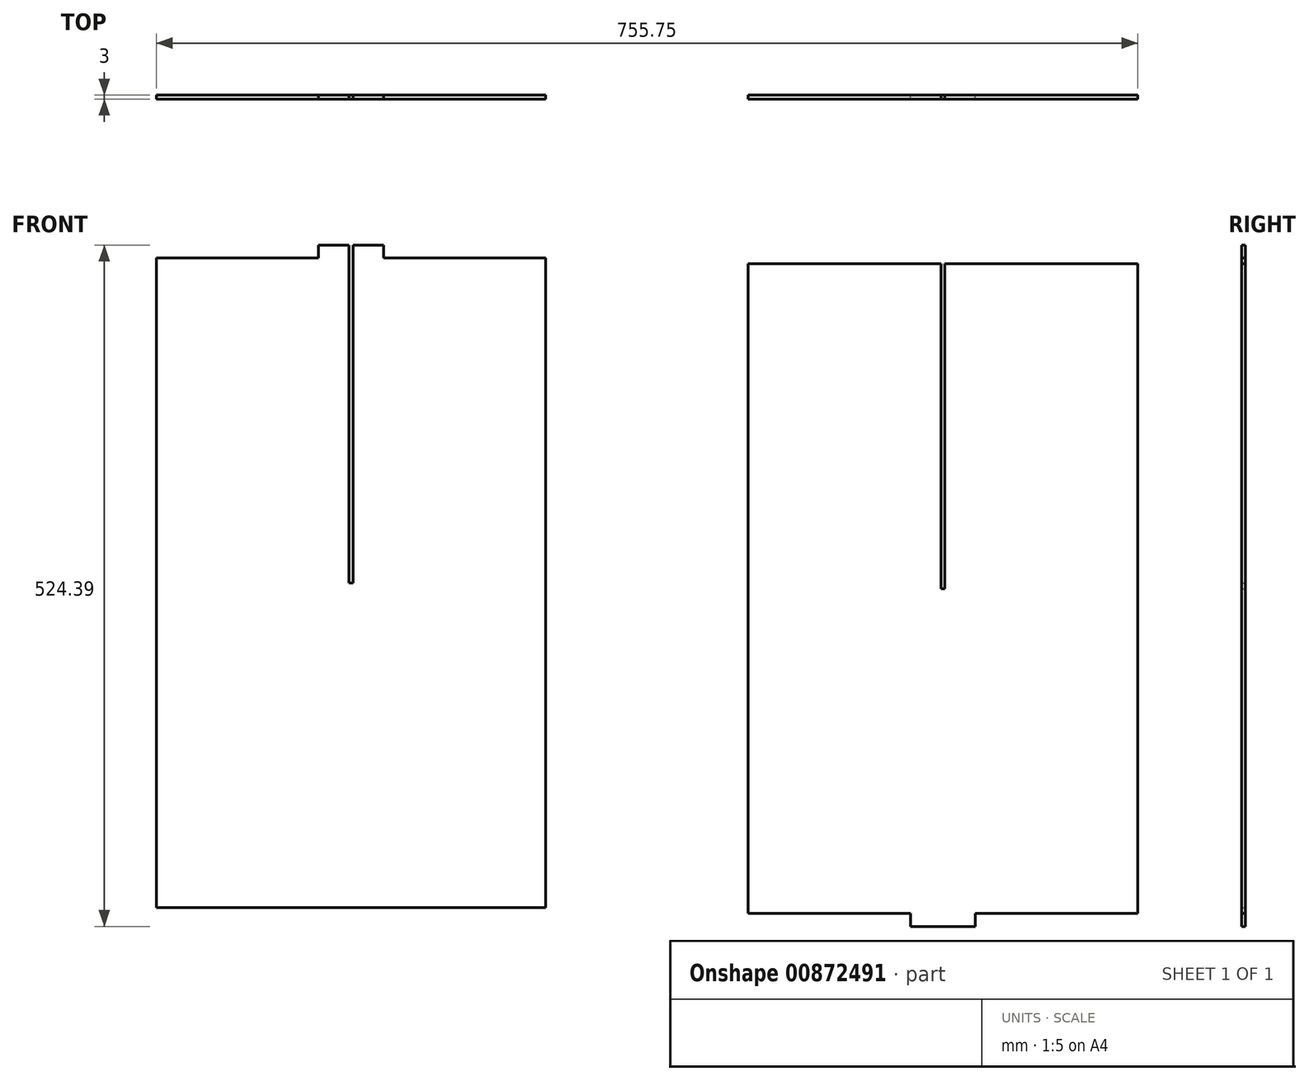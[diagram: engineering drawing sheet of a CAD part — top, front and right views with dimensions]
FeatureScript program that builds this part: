
annotation { "Feature Type Name" : "Feature", "Feature Type Description" : "" }
export const myFeature = defineFeature(function(context is Context, id is Id, definition is map)
    precondition{}
    {
        {
            var Q0;
            Q0=qCreatedBy(makeId("Front.planeOp"),FACE);
            var sketch = newSketch(context, id + "F0", { "sketchPlane" : qUnion([Q0])});
            skLineSegment(sketch, "E0.bottom", {"start": v(-150, -250) * mm, "end": v(150, -250) * mm});
            skLineSegment(sketch, "E0.top", {"start": v(-150, 250) * mm, "end": v(-25, 250) * mm});
            skLineSegment(sketch, "E0.left", {"start": v(-150, -250) * mm, "end": v(-150, 250) * mm});
            skLineSegment(sketch, "E0.right", {"start": v(150, -250) * mm, "end": v(150, 250) * mm});
            skPoint(sketch, "E0.middle", {"position": v(0, 0) * mm});
            skLineSegment(sketch, "E1.left", {"start": v(-1.5, 250) * mm, "end": v(-1.5, 250) * mm});
            skLineSegment(sketch, "E2.bottom", {"start": v(-1.5, 0) * mm, "end": v(1.5, 0) * mm});
            skLineSegment(sketch, "E2.left", {"start": v(-1.5, 0) * mm, "end": v(-1.5, 0) * mm});
            skLineSegment(sketch, "E2.right", {"start": v(1.5, 0) * mm, "end": v(1.5, 0) * mm});
            skLineSegment(sketch, "E3", {"start": v(-1.5, 250) * mm, "end": v(-1.5, 0) * mm});
            skLineSegment(sketch, "E4", {"start": v(1.5, 250) * mm, "end": v(1.5, 0) * mm});
            skLineSegment(sketch, "E5.trimOffspring", {"start": v(25, 250) * mm, "end": v(150, 250) * mm});
            skLineSegment(sketch, "E6.top", {"start": v(25, 260) * mm, "end": v(1.5, 260) * mm});
            skLineSegment(sketch, "E6.left", {"start": v(25, 260) * mm, "end": v(25, 250) * mm});
            skLineSegment(sketch, "E6.right", {"start": v(-25, 260) * mm, "end": v(-25, 250) * mm});
            skPoint(sketch, "E6.middle", {"position": v(0, 255) * mm});
            skPoint(sketch, "E1.right.start.orphan", {"position": v(1.5, 255) * mm});
            skLineSegment(sketch, "E7", {"start": v(-1.5, 250) * mm, "end": v(-1.5, 260) * mm});
            skLineSegment(sketch, "E8", {"start": v(1.5, 250) * mm, "end": v(1.5, 260) * mm});
            skLineSegment(sketch, "E9.trimOffspring", {"start": v(-1.5, 260) * mm, "end": v(-25, 260) * mm});
            skLineSegment(sketch, "E10.bottom", {"start": v(305.75, -254.39) * mm, "end": v(430.75, -254.39) * mm});
            skLineSegment(sketch, "E10.top", {"start": v(305.75, 245.61) * mm, "end": v(430.75, 245.61) * mm});
            skLineSegment(sketch, "E10.left", {"start": v(305.75, -254.39) * mm, "end": v(305.75, 245.61) * mm});
            skLineSegment(sketch, "E10.right", {"start": v(605.75, -254.39) * mm, "end": v(605.75, 245.61) * mm});
            skPoint(sketch, "E10.middle", {"position": v(455.75, -4.39) * mm});
            skLineSegment(sketch, "E11.bottom", {"start": v(454.25, -4.39) * mm, "end": v(457.25, -4.39) * mm});
            skLineSegment(sketch, "E12", {"start": v(454.25, 245.61) * mm, "end": v(454.25, -4.39) * mm});
            skLineSegment(sketch, "E13", {"start": v(457.25, 245.61) * mm, "end": v(457.25, -4.39) * mm});
            skLineSegment(sketch, "E14.trimOffspring", {"start": v(480.75, 245.61) * mm, "end": v(605.75, 245.61) * mm});
            skLineSegment(sketch, "E15.MirrorCS", {"start": v(480.75, -264.39) * mm, "end": v(480.75, -254.39) * mm});
            skLineSegment(sketch, "E16.MirrorCS", {"start": v(480.75, -264.39) * mm, "end": v(457.25, -264.39) * mm});
            skLineSegment(sketch, "E17.MirrorCS", {"start": v(454.25, -264.39) * mm, "end": v(430.75, -264.39) * mm});
            skLineSegment(sketch, "E18.MirrorCS", {"start": v(430.75, -264.39) * mm, "end": v(430.75, -254.39) * mm});
            skLineSegment(sketch, "E19", {"start": v(454.25, -264.39) * mm, "end": v(457.25, -264.39) * mm});
            skLineSegment(sketch, "E20.trimOffspring", {"start": v(480.75, -254.39) * mm, "end": v(605.75, -254.39) * mm});
            skLineSegment(sketch, "E21", {"start": v(430.75, 245.61) * mm, "end": v(454.25, 245.61) * mm});
            skLineSegment(sketch, "E22.trimOffspring", {"start": v(457.25, 245.61) * mm, "end": v(480.75, 245.61) * mm});
            skSolve(sketch);
        }
        {
            var Q0;
            Q0 = qSketchRegion(id + "F0", true);
            extrude(context, id + "F1", {"entities" : qUnion([Q0]), "depth" : 3 * mm, "offsetDistance" : 25 * mm});
        }
    });
